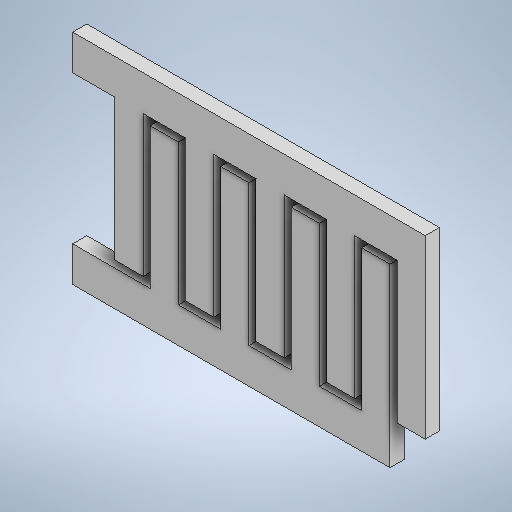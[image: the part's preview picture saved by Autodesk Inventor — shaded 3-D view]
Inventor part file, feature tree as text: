
AUTODESK INVENTOR PART (.ipt)
format: ipt  version: 2025.2 (Build 292293000, 293)  size: 278,528 bytes
history: native  units: mm
features: other x1, extrude x1, sketch x1
ambient origin geometry x8: Origin, YZ Plane, XZ Plane, XY Plane, X Axis, Y Axis, Z Axis, Center Point
bodies: Body1 (feature_tree)
feature tree (3):
  other  "Sólido1"
  extrude  "Extrusão1"  Depth=50.0mm
  sketch  "Esboço1"  dims[d5=5.0mm d6=50.0mm d7=15.0mm d9=25.0mm d10=4.0mm d12=6.0mm d33=2.0mm d34=0.0mm d37=5.0mm d43=1.0mm d45=1.0mm d31=0.5mm d32=0.872665mm]
